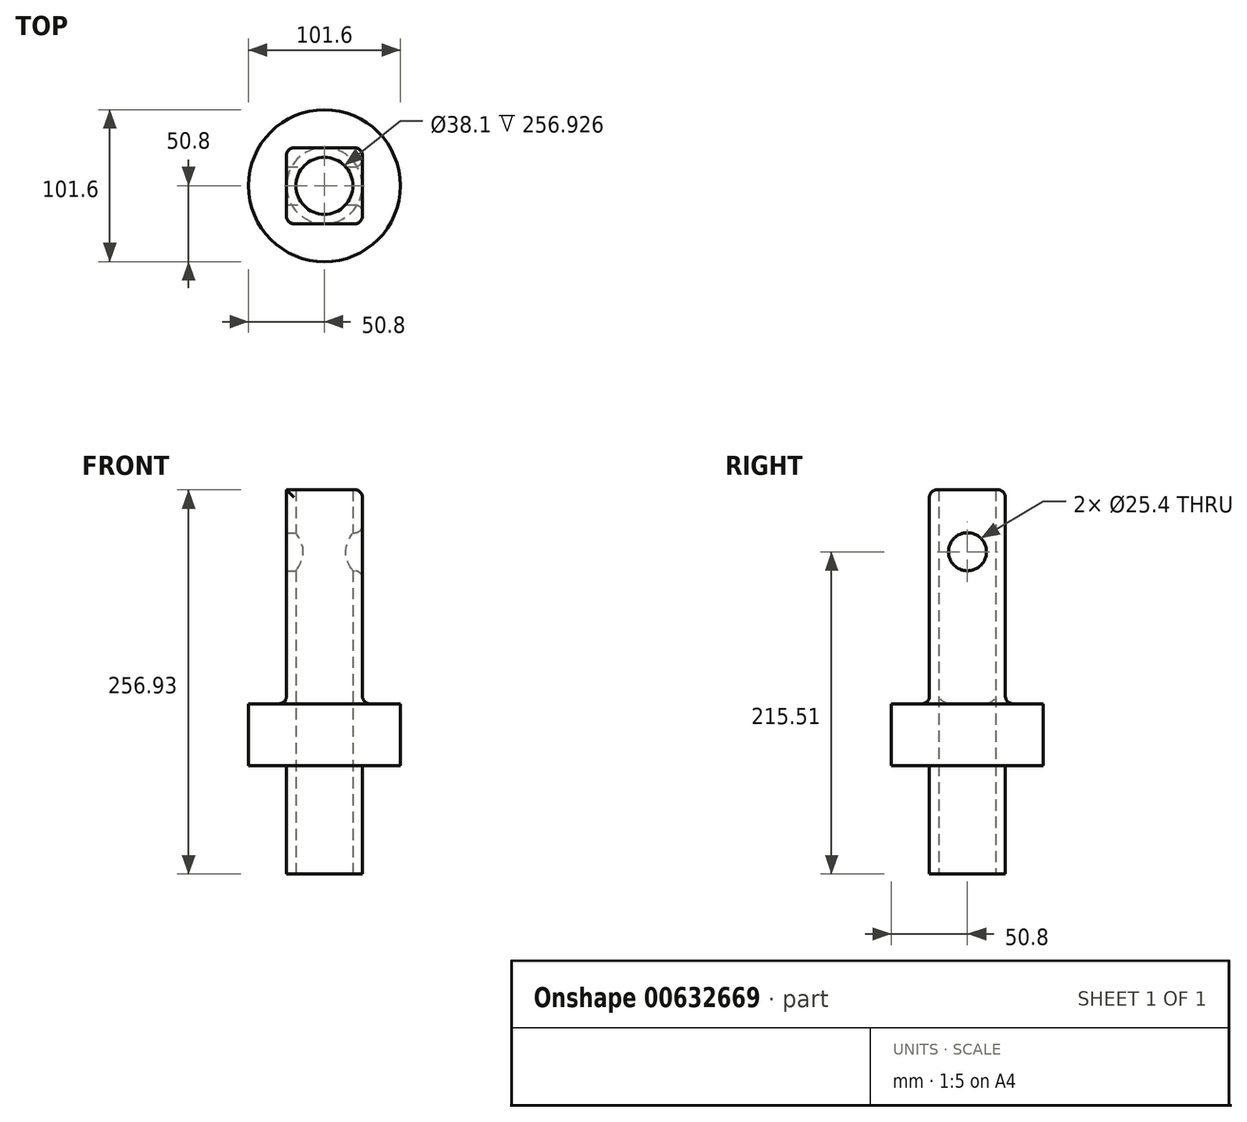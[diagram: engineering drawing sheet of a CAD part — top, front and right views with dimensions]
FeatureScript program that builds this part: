
annotation { "Feature Type Name" : "Feature", "Feature Type Description" : "" }
export const myFeature = defineFeature(function(context is Context, id is Id, definition is map)
    precondition{}
    {
        {
            var Q0;
            Q0=qCreatedBy(makeId("Top.planeOp"),FACE);
            var sketch = newSketch(context, id + "F0", { "sketchPlane" : qUnion([Q0])});
            skCircle(sketch, "E0", {"center": v(0, 0) * mm, "radius": 50.8 * mm});
            skSolve(sketch);
        }
        {
            var Q0;
            Q0=makeQuery(id+"F0.imprint","IMPRINT",FACE,{"disambiguationData":[TD([[makeQuery(id+"F0.imprint","IMPRINT",EDGE,{"derivedFrom":sQuery(id+"F0.wireOp",EDGE,"E0")}),1.0]])]});
            extrude(context, id + "F1", {"entities" : qUnion([Q0]), "oppositeDirection" : true, "depth" : 41.45 * mm, "offsetDistance" : 25.4 * mm});
        }
        {
            var Q0;
            Q0=makeQuery(id+"F1.opExtrude","CAP_FACE",FACE,{"disambiguationData":[OSD([sQuery(id+"F0.wireOp",EDGE,"E0")])],"isStart":true});
            var sketch = newSketch(context, id + "F2", { "sketchPlane" : qUnion([Q0])});
            skLineSegment(sketch, "E1.bottom", {"start": v(-25.4, 25.4) * mm, "end": v(25.4, 25.4) * mm});
            skLineSegment(sketch, "E1.top", {"start": v(-25.4, -25.4) * mm, "end": v(25.4, -25.4) * mm});
            skLineSegment(sketch, "E1.left", {"start": v(-25.4, 25.4) * mm, "end": v(-25.4, -25.4) * mm});
            skLineSegment(sketch, "E1.right", {"start": v(25.4, 25.4) * mm, "end": v(25.4, -25.4) * mm});
            skPoint(sketch, "E1.middle", {"position": v(0, 0) * mm});
            skSolve(sketch);
        }
        {
            var Q0;
            Q0 = qSketchRegion(id + "F2", true);
            extrude(context, id + "F3", {"entities" : qUnion([Q0]), "operationType" : NewBodyOperationType.ADD, "depth" : 143.02 * mm, "offsetDistance" : 25.4 * mm});
        }
        {
            var Q0;
            Q0=makeQuery(id+"F3.opExtrude","SWEPT_FACE",FACE,{"disambiguationData":[OSD([sQuery(id+"F2.wireOp",EDGE,"E1.right")])]});
            var sketch = newSketch(context, id + "F4", { "sketchPlane" : qUnion([Q0])});
            skCircle(sketch, "E2", {"center": v(0, 101.6) * mm, "radius": 12.7 * mm});
            skSolve(sketch);
        }
        {
            var Q0;
            Q0 = qSketchRegion(id + "F4", true);
            extrude(context, id + "F5", {"entities" : qUnion([Q0]), "operationType" : NewBodyOperationType.REMOVE, "endBound" : BoundingType.THROUGH_ALL, "oppositeDirection" : true, "depth" : 25.4 * mm, "offsetDistance" : 25.4 * mm});
        }
        {
            var Q0;
            Q0=makeQuery(id+"F3.opExtrude","SWEPT_FACE",FACE,{"disambiguationData":[OSD([sQuery(id+"F2.wireOp",EDGE,"E1.bottom")])]});
            var Q1;
            Q1=makeQuery(id+"F3.opExtrude","SWEPT_FACE",FACE,{"disambiguationData":[OSD([sQuery(id+"F2.wireOp",EDGE,"E1.right")])]});
            var Q2;
            Q2=makeQuery(id+"F3.opExtrude","SWEPT_FACE",FACE,{"disambiguationData":[OSD([sQuery(id+"F2.wireOp",EDGE,"E1.top")])]});
            fillet(context, id + "F6", {"entities" : qUnion([Q0, Q1, Q2]), "radius" : 5.08 * mm, "tangentPropagation" : true, "allowEdgeOverflow" : false});
        }
        {
            var Q0;
            Q0=makeQuery(id+"F1.opExtrude","CAP_FACE",FACE,{"disambiguationData":[OSD([sQuery(id+"F0.wireOp",EDGE,"E0")])],"isStart":false});
            var sketch = newSketch(context, id + "F7", { "sketchPlane" : qUnion([Q0])});
            skCircle(sketch, "E3", {"center": v(0, 0) * mm, "radius": 19.05 * mm});
            skSolve(sketch);
        }
        {
            var Q0;
            Q0 = qSketchRegion(id + "F7", true);
            extrude(context, id + "F8", {"entities" : qUnion([Q0]), "operationType" : NewBodyOperationType.REMOVE, "endBound" : BoundingType.THROUGH_ALL, "oppositeDirection" : true, "depth" : 25.4 * mm, "offsetDistance" : 25.4 * mm});
        }
        {
            var Q0;
            Q0=makeQuery(id+"F1.opExtrude","CAP_FACE",FACE,{"disambiguationData":[OSD([sQuery(id+"F0.wireOp",EDGE,"E0")])],"isStart":false});
            var sketch = newSketch(context, id + "F9", { "sketchPlane" : qUnion([Q0])});
            skCircle(sketch, "E4", {"center": v(0, 0) * mm, "radius": 25.4 * mm});
            skCircle(sketch, "E5", {"center": v(0, 0) * mm, "radius": 19.05 * mm});
            skSolve(sketch);
        }
        {
            var Q0;
            Q0 = qSketchRegion(id + "F9", true);
            extrude(context, id + "F10", {"entities" : qUnion([Q0]), "operationType" : NewBodyOperationType.ADD, "depth" : 72.46 * mm, "offsetDistance" : 25.4 * mm});
        }
    });
